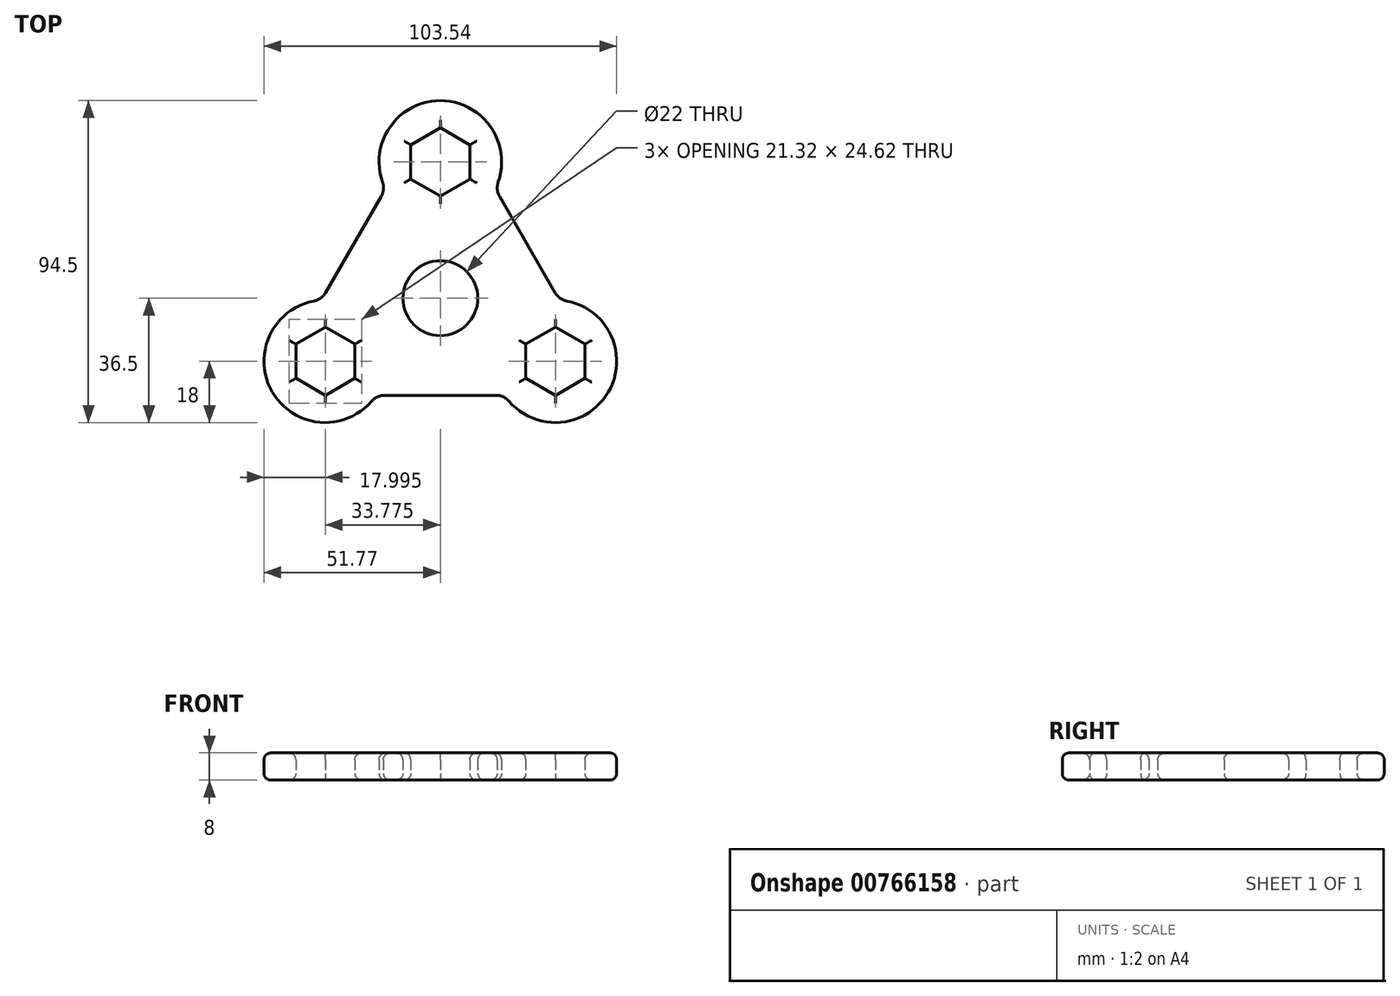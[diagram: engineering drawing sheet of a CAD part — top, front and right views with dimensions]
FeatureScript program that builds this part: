
annotation { "Feature Type Name" : "Feature", "Feature Type Description" : "" }
export const myFeature = defineFeature(function(context is Context, id is Id, definition is map)
    precondition{}
    {
        {
            var Q0;
            Q0=qCreatedBy(makeId("Top.planeOp"),FACE);
            var sketch = newSketch(context, id + "F0", { "sketchPlane" : qUnion([Q0])});
            skCircle(sketch, "E0", {"center": v(0, 0) * mm, "radius": 11 * mm});
            skLineSegment(sketch, "E1", {"start": v(0, 0) * mm, "end": v(0, 50) * mm, "construction": true});
            skLineSegment(sketch, "E2", {"start": v(0, 50) * mm, "end": v(0, 55) * mm, "construction": true});
            skCircle(sketch, "E3.cCircle", {"center": v(0, 40) * mm, "radius": 10 * mm, "construction": true});
            skLineSegment(sketch, "E3.0", {"start": v(-8.66, 45) * mm, "end": v(0, 50) * mm});
            skLineSegment(sketch, "E3.1", {"start": v(0, 50) * mm, "end": v(8.66, 45) * mm});
            skLineSegment(sketch, "E3.2", {"start": v(8.66, 45) * mm, "end": v(8.66, 35) * mm});
            skLineSegment(sketch, "E3.3", {"start": v(8.66, 35) * mm, "end": v(0, 30) * mm});
            skLineSegment(sketch, "E3.4", {"start": v(0, 30) * mm, "end": v(-8.66, 35) * mm});
            skLineSegment(sketch, "E3.5", {"start": v(-8.66, 35) * mm, "end": v(-8.66, 45) * mm});
            skLineSegment(sketch, "E4.1.0", {"start": v(0.87, 1.5) * mm, "end": v(-42.44, -23.5) * mm, "construction": true});
            skCircle(sketch, "E4.1.1", {"center": v(-33.77, -18.5) * mm, "radius": 10 * mm, "construction": true});
            skLineSegment(sketch, "E4.1.2", {"start": v(-33.77, -28.5) * mm, "end": v(-42.44, -23.5) * mm});
            skLineSegment(sketch, "E4.1.3", {"start": v(-25.11, -23.5) * mm, "end": v(-33.77, -28.5) * mm});
            skLineSegment(sketch, "E4.1.4", {"start": v(-25.11, -13.5) * mm, "end": v(-25.11, -23.5) * mm});
            skLineSegment(sketch, "E4.1.5", {"start": v(-33.77, -8.5) * mm, "end": v(-25.11, -13.5) * mm});
            skLineSegment(sketch, "E4.1.6", {"start": v(-42.44, -13.5) * mm, "end": v(-33.77, -8.5) * mm});
            skLineSegment(sketch, "E4.1.7", {"start": v(-42.44, -23.5) * mm, "end": v(-42.44, -13.5) * mm});
            skLineSegment(sketch, "E4.1.8", {"start": v(-42.44, -23.5) * mm, "end": v(-46.77, -26) * mm, "construction": true});
            skLineSegment(sketch, "E4.2.0", {"start": v(-0.87, 1.5) * mm, "end": v(42.44, -23.5) * mm, "construction": true});
            skCircle(sketch, "E4.2.1", {"center": v(33.77, -18.5) * mm, "radius": 10 * mm, "construction": true});
            skLineSegment(sketch, "E4.2.2", {"start": v(42.44, -13.5) * mm, "end": v(42.44, -23.5) * mm});
            skLineSegment(sketch, "E4.2.3", {"start": v(33.77, -8.5) * mm, "end": v(42.44, -13.5) * mm});
            skLineSegment(sketch, "E4.2.4", {"start": v(25.11, -13.5) * mm, "end": v(33.77, -8.5) * mm});
            skLineSegment(sketch, "E4.2.5", {"start": v(25.11, -23.5) * mm, "end": v(25.11, -13.5) * mm});
            skLineSegment(sketch, "E4.2.6", {"start": v(33.77, -28.5) * mm, "end": v(25.11, -23.5) * mm});
            skLineSegment(sketch, "E4.2.7", {"start": v(42.44, -23.5) * mm, "end": v(33.77, -28.5) * mm});
            skLineSegment(sketch, "E4.2.8", {"start": v(42.44, -23.5) * mm, "end": v(46.77, -26) * mm, "construction": true});
            skPoint(sketch, "E4.center", {"position": v(0, 1) * mm});
            skArc(sketch, "E5", {"start": v(-37.12, -0.81) * mm, "mid": v(-49.36, -27.5) * mm, "end": v(-20.13, -30.24) * mm});
            skArc(sketch, "E6", {"start": v(16.99, 34.05) * mm, "mid": v(0, 58) * mm, "end": v(-16.99, 34.05) * mm});
            skArc(sketch, "E7", {"start": v(20.13, -30.24) * mm, "mid": v(49.36, -27.5) * mm, "end": v(37.12, -0.81) * mm});
            skLineSegment(sketch, "E8", {"start": v(-33.72, 1.6) * mm, "end": v(-17.38, 29.9) * mm});
            skLineSegment(sketch, "E9", {"start": v(17.38, 29.9) * mm, "end": v(33.72, 1.6) * mm});
            skLineSegment(sketch, "E10", {"start": v(16.34, -28.5) * mm, "end": v(-16.34, -28.5) * mm});
            skPoint(sketch, "E11.visualSharp", {"position": v(-16.14, 32.04) * mm});
            skArc(sketch, "E11.filletArc", {"start": v(-17.38, 29.9) * mm, "mid": v(-16.73, 31.93) * mm, "end": v(-16.99, 34.05) * mm});
            skPoint(sketch, "E12.visualSharp", {"position": v(-34.95, -0.54) * mm});
            skArc(sketch, "E12.filletArc", {"start": v(-37.12, -0.81) * mm, "mid": v(-35.15, 0.02) * mm, "end": v(-33.72, 1.6) * mm});
            skPoint(sketch, "E13.visualSharp", {"position": v(-18.8, -28.5) * mm});
            skArc(sketch, "E13.filletArc", {"start": v(-16.34, -28.5) * mm, "mid": v(-18.42, -28.96) * mm, "end": v(-20.13, -30.24) * mm});
            skPoint(sketch, "E14.visualSharp", {"position": v(18.8, -28.5) * mm});
            skArc(sketch, "E14.filletArc", {"start": v(20.13, -30.24) * mm, "mid": v(18.42, -28.96) * mm, "end": v(16.34, -28.5) * mm});
            skPoint(sketch, "E15.visualSharp", {"position": v(34.95, -0.54) * mm});
            skArc(sketch, "E15.filletArc", {"start": v(33.72, 1.6) * mm, "mid": v(35.15, 0.02) * mm, "end": v(37.12, -0.81) * mm});
            skPoint(sketch, "E16.visualSharp", {"position": v(16.14, 32.04) * mm});
            skArc(sketch, "E16.filletArc", {"start": v(16.99, 34.05) * mm, "mid": v(16.73, 31.93) * mm, "end": v(17.38, 29.9) * mm});
            skSolve(sketch);
        }
        {
            var Q0;
            Q0 = qSketchRegion(id + "F0", true);
            extrude(context, id + "F1", {"entities" : qUnion([Q0]), "depth" : 8 * mm, "offsetDistance" : 25 * mm});
        }
        {
            var Q0;
            Q0=makeQuery(id+"F1.opExtrude","CAP_FACE",FACE,{"disambiguationData":[OSD([sQuery(id+"F0.wireOp",EDGE,"E0"),sQuery(id+"F0.wireOp",EDGE,"E3.0"),sQuery(id+"F0.wireOp",EDGE,"E3.1"),sQuery(id+"F0.wireOp",EDGE,"E3.2"),sQuery(id+"F0.wireOp",EDGE,"E3.3"),sQuery(id+"F0.wireOp",EDGE,"E3.4"),sQuery(id+"F0.wireOp",EDGE,"E3.5"),sQuery(id+"F0.wireOp",EDGE,"E4.1.2"),sQuery(id+"F0.wireOp",EDGE,"E4.1.3"),sQuery(id+"F0.wireOp",EDGE,"E4.1.4"),sQuery(id+"F0.wireOp",EDGE,"E4.1.5"),sQuery(id+"F0.wireOp",EDGE,"E4.1.6"),sQuery(id+"F0.wireOp",EDGE,"E4.1.7"),sQuery(id+"F0.wireOp",EDGE,"E4.2.2"),sQuery(id+"F0.wireOp",EDGE,"E4.2.3"),sQuery(id+"F0.wireOp",EDGE,"E4.2.4"),sQuery(id+"F0.wireOp",EDGE,"E4.2.5"),sQuery(id+"F0.wireOp",EDGE,"E4.2.6"),sQuery(id+"F0.wireOp",EDGE,"E4.2.7"),sQuery(id+"F0.wireOp",EDGE,"E5"),sQuery(id+"F0.wireOp",EDGE,"E6"),sQuery(id+"F0.wireOp",EDGE,"E7"),sQuery(id+"F0.wireOp",EDGE,"E8"),sQuery(id+"F0.wireOp",EDGE,"E9"),sQuery(id+"F0.wireOp",EDGE,"E10"),sQuery(id+"F0.wireOp",EDGE,"E11.filletArc"),sQuery(id+"F0.wireOp",EDGE,"E12.filletArc"),sQuery(id+"F0.wireOp",EDGE,"E13.filletArc"),sQuery(id+"F0.wireOp",EDGE,"E14.filletArc"),sQuery(id+"F0.wireOp",EDGE,"E15.filletArc"),sQuery(id+"F0.wireOp",EDGE,"E16.filletArc")])],"isStart":false});
            fillet(context, id + "F2", {"entities" : qUnion([Q0]), "radius" : 2 * mm, "tangentPropagation" : true, "allowEdgeOverflow" : false});
        }
        {
            var Q0;
            Q0=makeQuery(id+"F1.opExtrude","CAP_FACE",FACE,{"disambiguationData":[OSD([sQuery(id+"F0.wireOp",EDGE,"E0"),sQuery(id+"F0.wireOp",EDGE,"E3.0"),sQuery(id+"F0.wireOp",EDGE,"E3.1"),sQuery(id+"F0.wireOp",EDGE,"E3.2"),sQuery(id+"F0.wireOp",EDGE,"E3.3"),sQuery(id+"F0.wireOp",EDGE,"E3.4"),sQuery(id+"F0.wireOp",EDGE,"E3.5"),sQuery(id+"F0.wireOp",EDGE,"E4.1.2"),sQuery(id+"F0.wireOp",EDGE,"E4.1.3"),sQuery(id+"F0.wireOp",EDGE,"E4.1.4"),sQuery(id+"F0.wireOp",EDGE,"E4.1.5"),sQuery(id+"F0.wireOp",EDGE,"E4.1.6"),sQuery(id+"F0.wireOp",EDGE,"E4.1.7"),sQuery(id+"F0.wireOp",EDGE,"E4.2.2"),sQuery(id+"F0.wireOp",EDGE,"E4.2.3"),sQuery(id+"F0.wireOp",EDGE,"E4.2.4"),sQuery(id+"F0.wireOp",EDGE,"E4.2.5"),sQuery(id+"F0.wireOp",EDGE,"E4.2.6"),sQuery(id+"F0.wireOp",EDGE,"E4.2.7"),sQuery(id+"F0.wireOp",EDGE,"E5"),sQuery(id+"F0.wireOp",EDGE,"E6"),sQuery(id+"F0.wireOp",EDGE,"E7"),sQuery(id+"F0.wireOp",EDGE,"E8"),sQuery(id+"F0.wireOp",EDGE,"E9"),sQuery(id+"F0.wireOp",EDGE,"E10"),sQuery(id+"F0.wireOp",EDGE,"E11.filletArc"),sQuery(id+"F0.wireOp",EDGE,"E12.filletArc"),sQuery(id+"F0.wireOp",EDGE,"E13.filletArc"),sQuery(id+"F0.wireOp",EDGE,"E14.filletArc"),sQuery(id+"F0.wireOp",EDGE,"E15.filletArc"),sQuery(id+"F0.wireOp",EDGE,"E16.filletArc")])],"isStart":true});
            fillet(context, id + "F3", {"entities" : qUnion([Q0]), "radius" : 2 * mm, "tangentPropagation" : true, "allowEdgeOverflow" : false});
        }
    });
